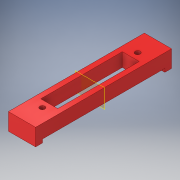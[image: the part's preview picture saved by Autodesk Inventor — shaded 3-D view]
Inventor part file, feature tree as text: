
AUTODESK INVENTOR PART (.ipt)
format: ipt  version: 2019 (Build 230136000, 136)  size: 136,704 bytes
history: native  units: in
note: dims shown in document units (in); Inventor stores cm internally (conversion verified against a paired STEP export)
features: extrude x4, sketch x4, mirror x2
ambient origin geometry x8: Origin, YZ Plane, XZ Plane, XY Plane, X Axis, Y Axis, Z Axis, Center Point
bodies: Solid1 (feature_tree)
feature tree (10):
  extrude  "Extrusion1"  Depth=10.0in
  extrude  "Extrusion2"  Depth=0.5in
  mirror  "Mirror1"
  extrude  "Extrusion3"  TaperAngle=0.0deg  [1 undecoded]
  mirror  "Mirror2"
  extrude  "Extrusion4"  Depth=0.375in
  sketch  "Sketch1"  dims[d0=2.0in d1=10.0in]
  sketch  "Sketch2"  dims[d2=1.0in d3=0.0in d4=0.5in]
  sketch  "Sketch3"  dims[d5=1.0in d6=0.0in]
  sketch  "Sketch4"  dims[d7=0.25in d8=0.0in d9=0.375in d10=1.5in d11=0.25in d12=0.0in d13=0.375in d14=2.0in d15=1.0in d16=0.0in]
note: 1 required parameter value undecoded (feature->parameter linkage not recoverable at this tier; creation-order binding heuristic only, values carry confidence <= 0.55)
